# Revit family: QF_ELECTROLUXPROFESSIONAL_1LSNLE_IC64825R_G
name_source: partatom
category: Attrezzature speciali
units: mm (PartAtom-declared; Revit-internal decimal feet)

## family parameters
Basato su piano di lavoro = No
Condiviso = No
Punto di calcolo locali = No
Quota connettore circolare = Usa diametro
Sempre verticale = Sì
Taglio con vuoti quando caricato = No
Tipo di parte = Normale

## types (4) — shared parameters
-B/2 = -1270 mm  [stored -4.16667 ft]
A_Width = 3205 mm
B_2 = 1270 mm  [stored 4.16667 ft]
B_IronerWidth = 2540 mm
C_WithBetweenFeet = 2930 mm  [stored 9.61286 ft]
Depth Actual = 1620 mm
DepthMax = 1100 mm
DepthPedestal = 950 mm  [stored 3.1168 ft]
Feet = 80 mm  [stored 0.262467 ft]
Gas KW = 52
Height = 1270 mm  [stored 4.16667 ft]
Height Actual = 1270 mm  [stored 4.16667 ft]
Latent Heat Output = 0.0
Length Actual = 3205 mm
Modello = IC64825R
Phase = 3
Produttore = Electrolux Professional
Sensible Heat Output = 0.0
URL = www.electroluxprofessional.com
Weight = 1025
zero-valued in all types: Prospetto di default, Steam Pounds per Hour

## per-type parameters (varying)
| type | Cycle | Descrizione | Item Number | Volts | Watts |
| 9882030308 | 50 Hz | IRONER CYLINDER IC64825R REAR DELIVERY 2540MM PERFORMANCE GAS CE 400/50/3 DUBIXIUM ML VAC.FEED.TABLE | 1LT68V | 400 V | 1200 W |
| 9882030276 | 60 Hz | IRONER CYLINDER IC64825R REAR DELIVERY 2540MM ACTIVE GAS CE 208-240/60/3 6MM SST CYL. EN, ES, PO FEED NOW | 1L0H8S | 240 V | 1400 W |
| 9882030299 | 50 Hz | IRONER CYLINDER IC64825R REAR DELIVERY 2540MM GAS CE 400/50/3 6MM SST CYL. ML DIAMMS | 1LA268 | 400 V | 1200 W |
| 9882030307 | 50 Hz | IRONER CYLINDER IC64825R REAR DELIVERY 2540MM ACTIVE GAS CE 400/50/3 6MM SST CYL. ML FEED NOW | 1LT68U | 400 V | 1200 W |

note: [stored X ft] marks values corroborated as IEEE doubles in the binary element streams (Revit-internal decimal feet)

## geometry (parser evidence)
native form markers: Sweep x12
no freeform markers — native parametric forms only
